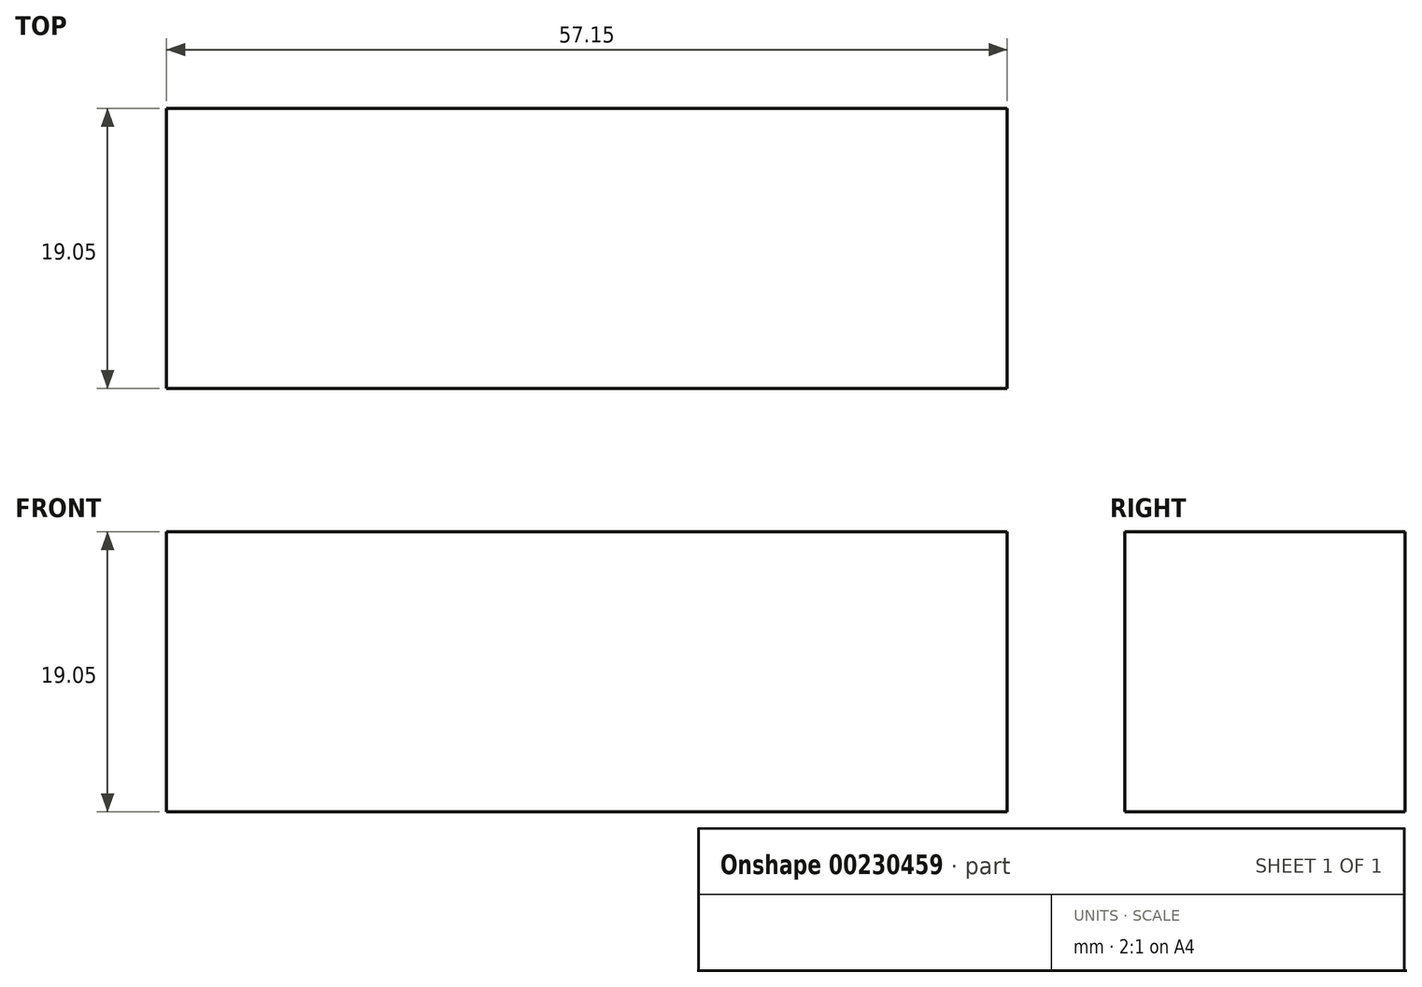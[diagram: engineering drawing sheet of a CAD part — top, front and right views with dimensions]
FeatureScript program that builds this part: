
annotation { "Feature Type Name" : "Feature", "Feature Type Description" : "" }
export const myFeature = defineFeature(function(context is Context, id is Id, definition is map)
    precondition{}
    {
        {
            var Q0;
            Q0=qCreatedBy(makeId("Front.planeOp"),FACE);
            var sketch = newSketch(context, id + "F0", { "sketchPlane" : qUnion([Q0])});
            skLineSegment(sketch, "E0.bottom", {"start": v(-36.35, 28.52) * mm, "end": v(20.8, 28.52) * mm});
            skLineSegment(sketch, "E0.top", {"start": v(-36.35, 9.47) * mm, "end": v(20.8, 9.47) * mm});
            skLineSegment(sketch, "E0.left", {"start": v(-36.35, 28.52) * mm, "end": v(-36.35, 9.47) * mm});
            skLineSegment(sketch, "E0.right", {"start": v(20.8, 28.52) * mm, "end": v(20.8, 9.47) * mm});
            skLineSegment(sketch, "E1.bottom", {"start": v(2.66, 9.47) * mm, "end": v(-16.39, 9.47) * mm});
            skLineSegment(sketch, "E1.top", {"start": v(2.66, -9.58) * mm, "end": v(-16.39, -9.58) * mm});
            skLineSegment(sketch, "E1.left", {"start": v(2.66, 9.47) * mm, "end": v(2.66, -9.58) * mm});
            skLineSegment(sketch, "E1.right", {"start": v(-16.39, 9.47) * mm, "end": v(-16.39, -9.58) * mm});
            skSolve(sketch);
        }
        {
            var Q0;
            Q0=makeQuery(id+"F0.imprint","IMPRINT",FACE,{"disambiguationData":[TD([[makeQuery(id+"F0.imprint","IMPRINT",EDGE,{"derivedFrom":sQuery(id+"F0.wireOp",EDGE,"E1.bottom")}),1.0]])]});
            var Q1;
            Q1=makeQuery(id+"F0.imprint","IMPRINT",FACE,{"disambiguationData":[TD([[makeQuery(id+"F0.imprint","IMPRINT",EDGE,{"derivedFrom":sQuery(id+"F0.wireOp",EDGE,"E0.bottom")}),-1.0]])]});
            extrude(context, id + "F1", {"entities" : qUnion([Q0, Q1]), "depth" : 19.05 * mm});
        }
    });
